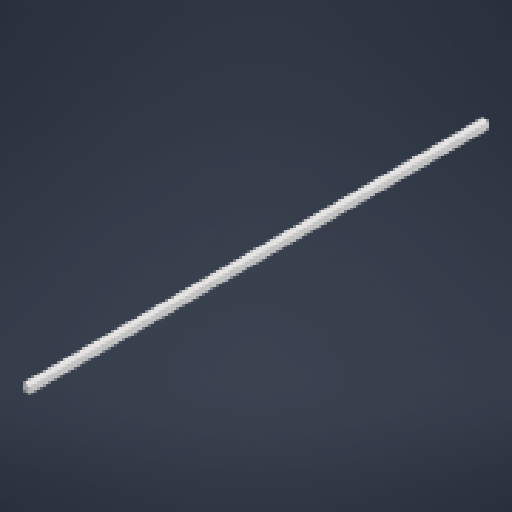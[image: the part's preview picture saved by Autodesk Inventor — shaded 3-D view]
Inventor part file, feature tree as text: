
AUTODESK INVENTOR PART (.ipt)
format: ipt  version: 2023 (Build 270158000, 158)  size: 140,288 bytes
history: native  units: in
note: dims shown in document units (in); Inventor stores cm internally (conversion verified against a paired STEP export)
features: sketch x2, extrude x1, hole x1
ambient origin geometry x8: Origin, YZ Plane, XZ Plane, XY Plane, X Axis, Y Axis, Z Axis, Center Point
bodies: Solid1 (feature_tree)
feature tree (4):
  extrude  "Extrusion1"  Depth=2.0in
  hole  "Hole2"  [1 undecoded]
  sketch  "Sketch1"  dims[d0=6.0in d1=2.0in]
  sketch  "Sketch3"  dims[d2=0.47in d3=0.0in d4=1.5in d5=1.5in d6=0.1875in d7=0.1875in d19=1.5in d20=1.5in d21=180.0deg d22=0.1875in d23=0.1875in d24=0.1875in d25=0.75in d26=0.375in d27=0.25in d28=0.5635in d29=1.0in d30=0.8108in]
note: 1 required parameter value undecoded (feature->parameter linkage not recoverable at this tier; creation-order binding heuristic only, values carry confidence <= 0.55)
